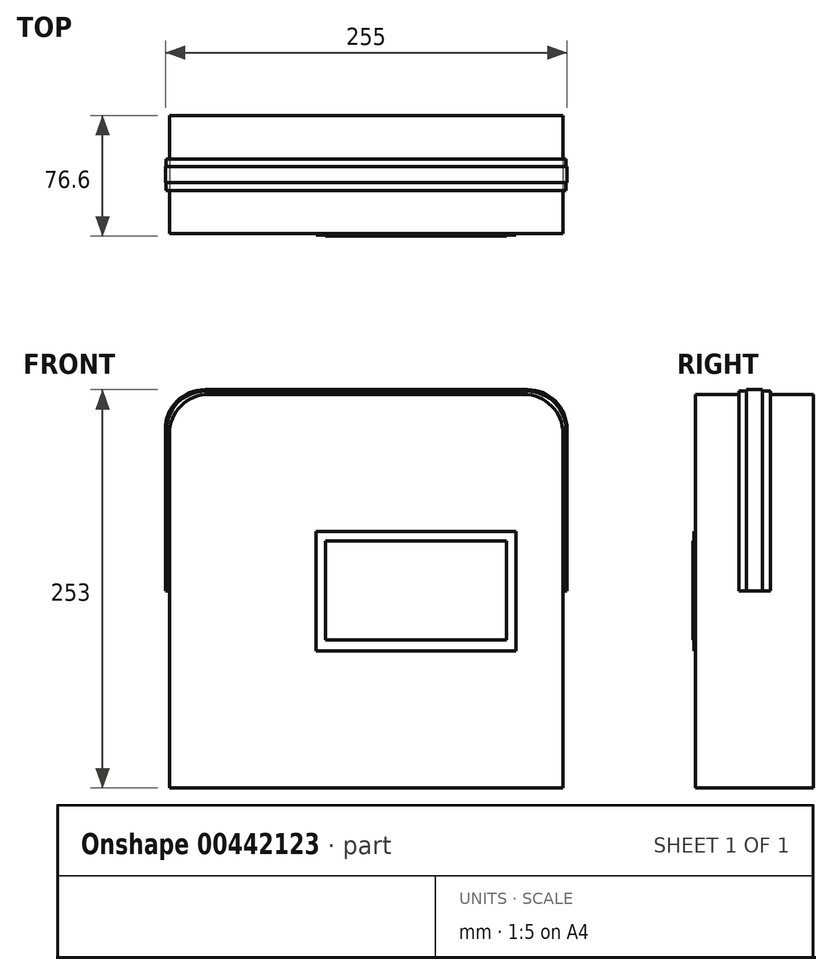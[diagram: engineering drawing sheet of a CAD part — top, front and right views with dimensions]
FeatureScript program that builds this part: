
annotation { "Feature Type Name" : "Feature", "Feature Type Description" : "" }
export const myFeature = defineFeature(function(context is Context, id is Id, definition is map)
    precondition{}
    {
        {
            var Q0;
            Q0=qCreatedBy(makeId("Top.planeOp"),FACE);
            var sketch = newSketch(context, id + "F0", { "sketchPlane" : qUnion([Q0])});
            skLineSegment(sketch, "E0.bottom", {"start": v(-125, 37.5) * mm, "end": v(125, 37.5) * mm});
            skLineSegment(sketch, "E0.top", {"start": v(-125, -37.5) * mm, "end": v(125, -37.5) * mm});
            skLineSegment(sketch, "E0.left", {"start": v(-125, 37.5) * mm, "end": v(-125, -37.5) * mm});
            skLineSegment(sketch, "E0.right", {"start": v(125, 37.5) * mm, "end": v(125, -37.5) * mm});
            skPoint(sketch, "E0.middle", {"position": v(0, 0) * mm});
            skSolve(sketch);
        }
        {
            var Q0;
            Q0=qCreatedBy(makeId("Top.planeOp"),FACE);
            var sketch = newSketch(context, id + "F1", { "sketchPlane" : qUnion([Q0])});
            skLineSegment(sketch, "E1.bottom", {"start": v(127, 10) * mm, "end": v(-127, 10) * mm});
            skLineSegment(sketch, "E1.top", {"start": v(127, -10) * mm, "end": v(-127, -10) * mm});
            skLineSegment(sketch, "E1.left", {"start": v(127, 10) * mm, "end": v(127, -10) * mm});
            skLineSegment(sketch, "E1.right", {"start": v(-127, 10) * mm, "end": v(-127, -10) * mm});
            skPoint(sketch, "E1.middle", {"position": v(0, 0) * mm});
            skSolve(sketch);
        }
        {
            var Q0;
            Q0 = qSketchRegion(id + "F0", true);
            extrude(context, id + "F2", {"entities" : qUnion([Q0]), "endBound" : BoundingType.SYMMETRIC, "depth" : 250 * mm});
        }
        {
            var Q0;
            Q0 = qSketchRegion(id + "F1", true);
            extrude(context, id + "F3", {"entities" : qUnion([Q0]), "operationType" : NewBodyOperationType.ADD, "depth" : 127 * mm});
        }
        {
            var Q0;
            Q0=makeQuery(id+"F3.opExtrude","CAP_EDGE",EDGE,{"disambiguationData":[OSD([sQuery(id+"F1.wireOp",EDGE,"E1.right")])],"isStart":false});
            var Q1;
            {var subQ0=sQuery(id+"F0.wireOp",EDGE,"E0.left");var subQ1=sQuery(id+"F0.wireOp",EDGE,"E0.top");Q1=makeQuery(id+"F3.boolean.opBoolean","SPLIT",EDGE,{"disambiguationData":[TD([makeQuery(id+"F2.opExtrude","SWEPT_FACE",FACE,{"disambiguationData":[OSD([subQ1])]})])],"derivedFrom":makeQuery(id+"F2.opExtrude","CAP_EDGE",EDGE,{"disambiguationData":[OSD([subQ0])],"isStart":false})});}
            var Q2;
            {var subQ0=sQuery(id+"F0.wireOp",EDGE,"E0.bottom");var subQ1=sQuery(id+"F0.wireOp",EDGE,"E0.right");Q2=makeQuery(id+"F3.boolean.opBoolean","SPLIT",EDGE,{"disambiguationData":[TD([makeQuery(id+"F2.opExtrude","SWEPT_FACE",FACE,{"disambiguationData":[OSD([subQ0])]})])],"derivedFrom":makeQuery(id+"F2.opExtrude","CAP_EDGE",EDGE,{"disambiguationData":[OSD([subQ1])],"isStart":false})});}
            var Q3;
            Q3=makeQuery(id+"F3.opExtrude","CAP_EDGE",EDGE,{"disambiguationData":[OSD([sQuery(id+"F1.wireOp",EDGE,"E1.left")])],"isStart":false});
            var Q4;
            {var subQ0=sQuery(id+"F0.wireOp",EDGE,"E0.right");var subQ1=sQuery(id+"F0.wireOp",EDGE,"E0.top");Q4=makeQuery(id+"F3.boolean.opBoolean","SPLIT",EDGE,{"disambiguationData":[TD([makeQuery(id+"F2.opExtrude","SWEPT_FACE",FACE,{"disambiguationData":[OSD([subQ1])]})])],"derivedFrom":makeQuery(id+"F2.opExtrude","CAP_EDGE",EDGE,{"disambiguationData":[OSD([subQ0])],"isStart":false})});}
            var Q5;
            {var subQ0=sQuery(id+"F0.wireOp",EDGE,"E0.bottom");var subQ1=sQuery(id+"F0.wireOp",EDGE,"E0.left");Q5=makeQuery(id+"F3.boolean.opBoolean","SPLIT",EDGE,{"disambiguationData":[TD([makeQuery(id+"F2.opExtrude","SWEPT_FACE",FACE,{"disambiguationData":[OSD([subQ0])]})])],"derivedFrom":makeQuery(id+"F2.opExtrude","CAP_EDGE",EDGE,{"disambiguationData":[OSD([subQ1])],"isStart":false})});}
            fillet(context, id + "F4", {"entities" : qUnion([Q0, Q1, Q2, Q3, Q4, Q5]), "radius" : 25 * mm, "tangentPropagation" : true, "allowEdgeOverflow" : false});
        }
        {
            var Q0;
            Q0=qCreatedBy(makeId("Top.planeOp"),FACE);
            var sketch = newSketch(context, id + "F5", { "sketchPlane" : qUnion([Q0])});
            skLineSegment(sketch, "E2.bottom", {"start": v(-127.5, 5) * mm, "end": v(127.5, 5) * mm});
            skLineSegment(sketch, "E2.top", {"start": v(-127.5, -5) * mm, "end": v(127.5, -5) * mm});
            skLineSegment(sketch, "E2.left", {"start": v(-127.5, 5) * mm, "end": v(-127.5, -5) * mm});
            skLineSegment(sketch, "E2.right", {"start": v(127.5, 5) * mm, "end": v(127.5, -5) * mm});
            skPoint(sketch, "E2.middle", {"position": v(0, 0) * mm});
            skSolve(sketch);
        }
        {
            var Q0;
            Q0 = qSketchRegion(id + "F5", true);
            extrude(context, id + "F6", {"entities" : qUnion([Q0]), "operationType" : NewBodyOperationType.ADD, "depth" : 128 * mm});
        }
        {
            var Q0;
            Q0=makeQuery(id+"F6.opExtrude","CAP_EDGE",EDGE,{"disambiguationData":[OSD([sQuery(id+"F5.wireOp",EDGE,"E2.left")])],"isStart":false});
            var Q1;
            Q1=makeQuery(id+"F6.opExtrude","CAP_EDGE",EDGE,{"disambiguationData":[OSD([sQuery(id+"F5.wireOp",EDGE,"E2.right")])],"isStart":false});
            fillet(context, id + "F7", {"entities" : qUnion([Q0, Q1]), "radius" : 25 * mm, "tangentPropagation" : true, "allowEdgeOverflow" : false});
        }
        {
            var Q0;
            Q0=makeQuery(id+"F2.opExtrude","SWEPT_FACE",FACE,{"disambiguationData":[OSD([sQuery(id+"F0.wireOp",EDGE,"E0.top")])]});
            var sketch = newSketch(context, id + "F8", { "sketchPlane" : qUnion([Q0])});
            skLineSegment(sketch, "E3.bottom", {"start": v(-32, -38) * mm, "end": v(95, -38) * mm});
            skLineSegment(sketch, "E3.top", {"start": v(-32, 38) * mm, "end": v(95, 38) * mm});
            skLineSegment(sketch, "E3.left", {"start": v(-32, -38) * mm, "end": v(-32, 38) * mm});
            skLineSegment(sketch, "E3.right", {"start": v(95, -38) * mm, "end": v(95, 38) * mm});
            skSolve(sketch);
        }
        {
            var Q0;
            Q0=makeQuery(id+"F8.imprint","IMPRINT",FACE,{"disambiguationData":[TD([[makeQuery(id+"F8.imprint","IMPRINT",EDGE,{"derivedFrom":sQuery(id+"F8.wireOp",EDGE,"E3.bottom")}),1.0]])]});
            extrude(context, id + "F9", {"entities" : qUnion([Q0]), "operationType" : NewBodyOperationType.ADD, "depth" : 1 * mm});
        }
        {
            var Q0;
            Q0=makeQuery(id+"F9.opExtrude","CAP_FACE",FACE,{"disambiguationData":[OSD([sQuery(id+"F8.wireOp",EDGE,"E3.bottom"),sQuery(id+"F8.wireOp",EDGE,"E3.top"),sQuery(id+"F8.wireOp",EDGE,"E3.left"),sQuery(id+"F8.wireOp",EDGE,"E3.right")])],"isStart":false});
            var sketch = newSketch(context, id + "F10", { "sketchPlane" : qUnion([Q0])});
            skLineSegment(sketch, "E4.bottom", {"start": v(-26, -31) * mm, "end": v(89, -31) * mm});
            skLineSegment(sketch, "E4.top", {"start": v(-26, 32) * mm, "end": v(89, 32) * mm});
            skLineSegment(sketch, "E4.left", {"start": v(-26, -31) * mm, "end": v(-26, 32) * mm});
            skLineSegment(sketch, "E4.right", {"start": v(89, -31) * mm, "end": v(89, 32) * mm});
            skLineSegment(sketch, "E5", {"start": v(-26, 32) * mm, "end": v(-13.5, 26) * mm});
            skLineSegment(sketch, "E6", {"start": v(-13.5, 26) * mm, "end": v(76.5, 26) * mm});
            skLineSegment(sketch, "E7", {"start": v(76.5, 26) * mm, "end": v(89, 32) * mm});
            skSolve(sketch);
        }
        {
            var Q0;
            Q0=makeQuery(id+"F10.imprint","IMPRINT",FACE,{"disambiguationData":[TD([[makeQuery(id+"F10.imprint","IMPRINT",EDGE,{"derivedFrom":sQuery(id+"F10.wireOp",EDGE,"E4.bottom")}),1.0]])]});
            var Q1;
            Q1=makeQuery(id+"F10.imprint","IMPRINT",FACE,{"disambiguationData":[TD([[makeQuery(id+"F10.imprint","IMPRINT",EDGE,{"derivedFrom":sQuery(id+"F10.wireOp",EDGE,"E4.top")}),-1.0]])]});
            extrude(context, id + "F11", {"entities" : qUnion([Q0, Q1]), "operationType" : NewBodyOperationType.ADD, "depth" : 0.6 * mm});
        }
    });
